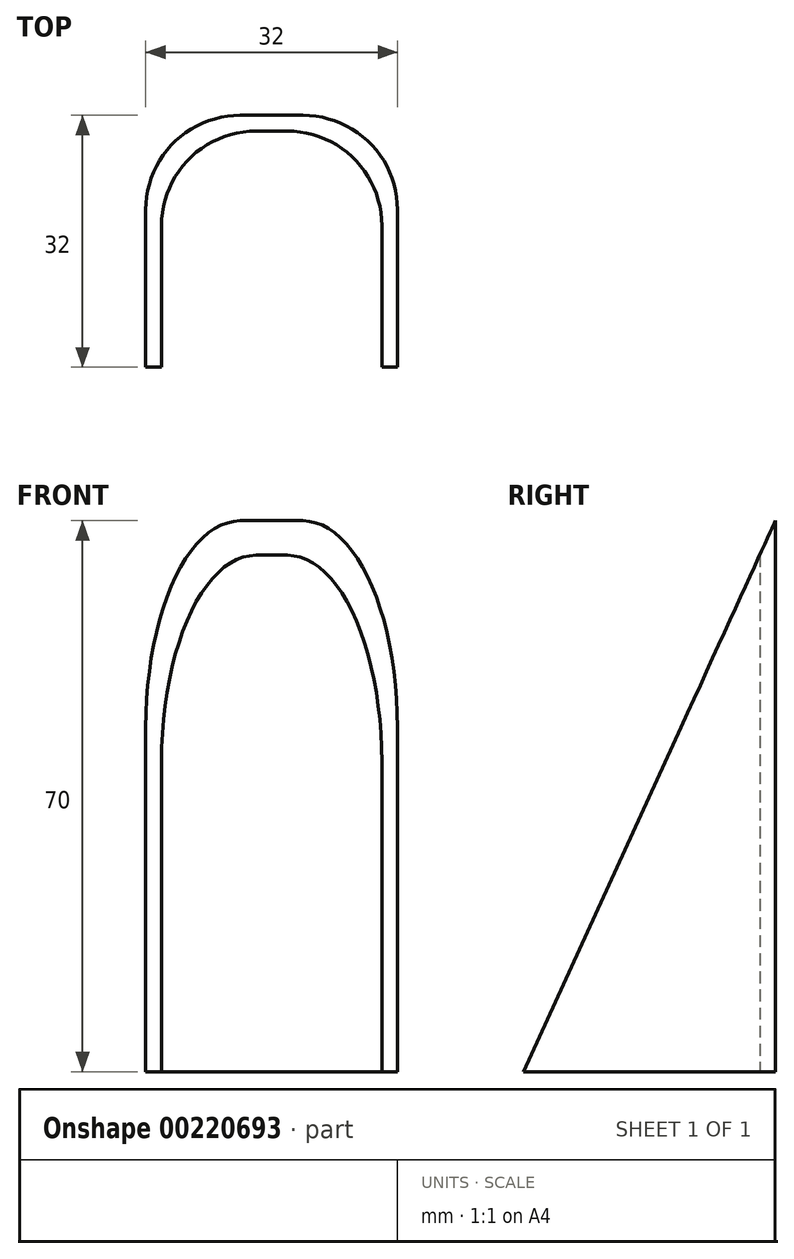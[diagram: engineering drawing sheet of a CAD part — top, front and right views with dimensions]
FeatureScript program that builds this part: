
annotation { "Feature Type Name" : "Feature", "Feature Type Description" : "" }
export const myFeature = defineFeature(function(context is Context, id is Id, definition is map)
    precondition{}
    {
        {
            var Q0;
            Q0=qCreatedBy(makeId("Top.planeOp"),FACE);
            var sketch = newSketch(context, id + "F0", { "sketchPlane" : qUnion([Q0])});
            skLineSegment(sketch, "E0.bottom", {"start": v(16, -16) * mm, "end": v(-16, -16) * mm});
            skLineSegment(sketch, "E0.top", {"start": v(16, 16) * mm, "end": v(-16, 16) * mm});
            skLineSegment(sketch, "E0.left", {"start": v(16, -16) * mm, "end": v(16, 16) * mm});
            skLineSegment(sketch, "E0.right", {"start": v(-16, -16) * mm, "end": v(-16, 16) * mm});
            skPoint(sketch, "E0.middle", {"position": v(0, 0) * mm});
            skLineSegment(sketch, "E1.bottom", {"start": v(-14, -16) * mm, "end": v(14, -16) * mm});
            skLineSegment(sketch, "E1.top", {"start": v(-14, 14) * mm, "end": v(14, 14) * mm});
            skLineSegment(sketch, "E1.left", {"start": v(-14, -16) * mm, "end": v(-14, 14) * mm});
            skLineSegment(sketch, "E1.right", {"start": v(14, -16) * mm, "end": v(14, 14) * mm});
            skSolve(sketch);
        }
        {
            var Q0;
            Q0=makeQuery(id+"F0.imprint","IMPRINT",FACE,{"disambiguationData":[TD([[makeQuery(id+"F0.imprint","IMPRINT",EDGE,{"derivedFrom":sQuery(id+"F0.wireOp",EDGE,"E0.top")}),1.0]])]});
            extrude(context, id + "F1", {"entities" : qUnion([Q0]), "depth" : 70 * mm});
        }
        {
            var Q0;
            Q0=makeQuery(id+"F1.opExtrude","SWEPT_FACE",FACE,{"disambiguationData":[OSD([sQuery(id+"F0.wireOp",EDGE,"E0.right")])]});
            var sketch = newSketch(context, id + "F2", { "sketchPlane" : qUnion([Q0])});
            skLineSegment(sketch, "E2", {"start": v(-16, 70) * mm, "end": v(16, 0) * mm});
            skLineSegment(sketch, "E3", {"start": v(16, 0) * mm, "end": v(16, 70) * mm});
            skLineSegment(sketch, "E4", {"start": v(16, 70) * mm, "end": v(-16, 70) * mm});
            skSolve(sketch);
        }
        {
            var Q0;
            Q0=makeQuery(id+"F2.imprint","IMPRINT",FACE,{"disambiguationData":[TD([[makeQuery(id+"F2.imprint","IMPRINT",EDGE,{"derivedFrom":sQuery(id+"F2.wireOp",EDGE,"E2")}),1.0]])]});
            extrude(context, id + "F3", {"entities" : qUnion([Q0]), "operationType" : NewBodyOperationType.REMOVE, "oppositeDirection" : true, "depth" : 33 * mm});
        }
        {
            var Q0;
            Q0=makeQuery(id+"F1.opExtrude","SWEPT_EDGE",EDGE,{"disambiguationData":[OSD([sQuery(id+"F0.wireOp",EDGE,"E0.top"),sQuery(id+"F0.wireOp",EDGE,"E0.left")])]});
            var Q1;
            Q1=makeQuery(id+"F1.opExtrude","SWEPT_EDGE",EDGE,{"disambiguationData":[OSD([sQuery(id+"F0.wireOp",EDGE,"E0.top"),sQuery(id+"F0.wireOp",EDGE,"E0.right")])]});
            var Q2;
            Q2=makeQuery(id+"F1.opExtrude","SWEPT_EDGE",EDGE,{"disambiguationData":[OSD([sQuery(id+"F0.wireOp",EDGE,"E1.top"),sQuery(id+"F0.wireOp",EDGE,"E1.left")])]});
            var Q3;
            Q3=makeQuery(id+"F1.opExtrude","SWEPT_EDGE",EDGE,{"disambiguationData":[OSD([sQuery(id+"F0.wireOp",EDGE,"E1.top"),sQuery(id+"F0.wireOp",EDGE,"E1.right")])]});
            fillet(context, id + "F4", {"entities" : qUnion([Q0, Q1, Q2, Q3]), "radius" : 12 * mm, "tangentPropagation" : true, "allowEdgeOverflow" : false});
        }
    });
